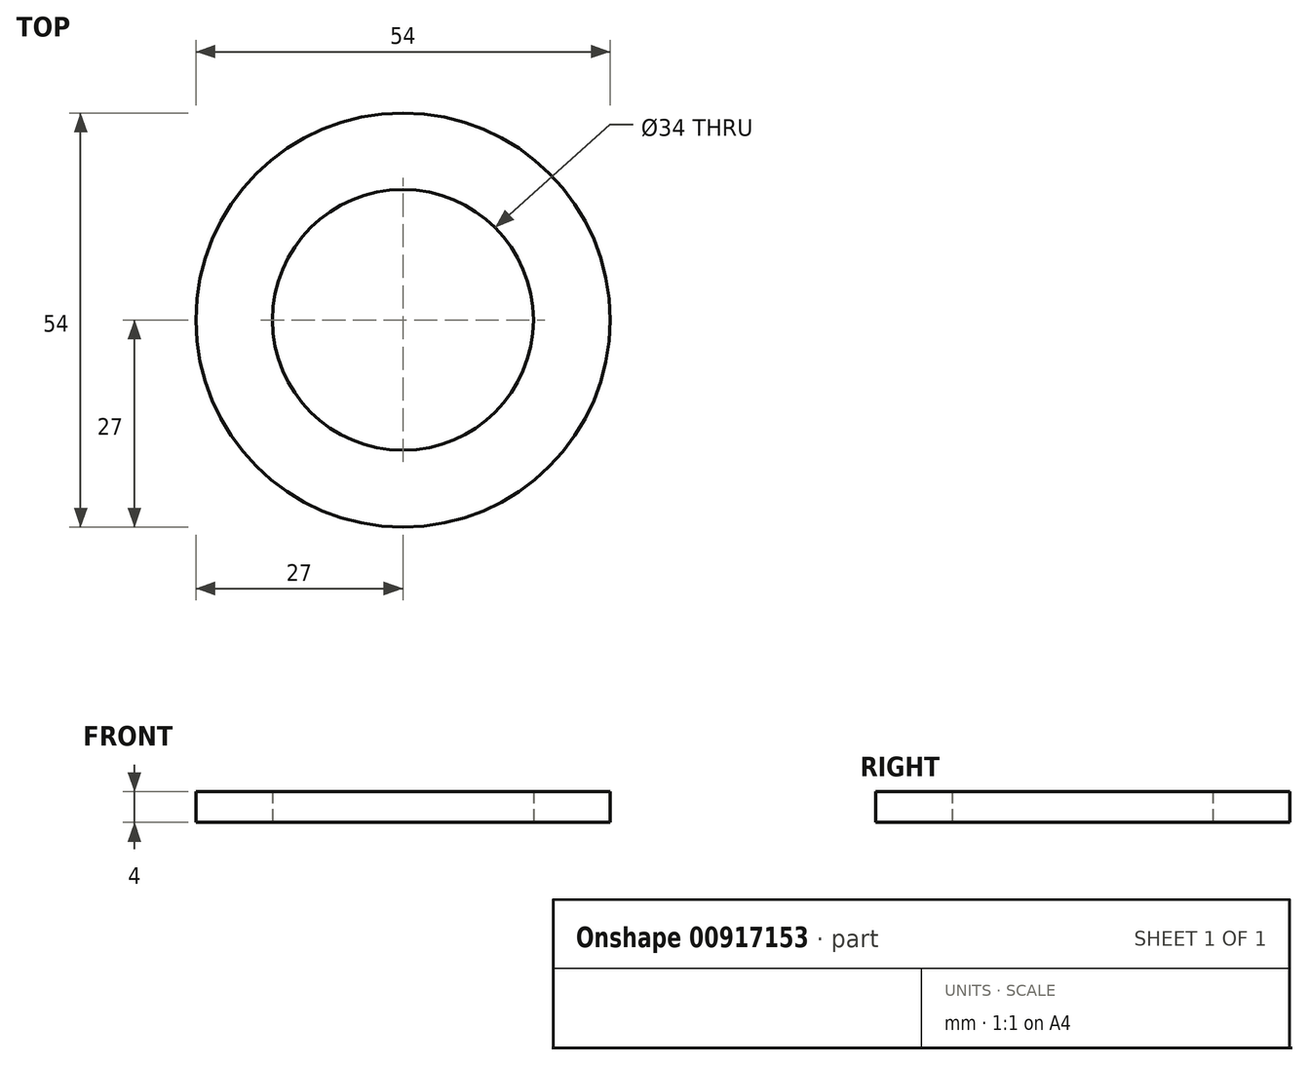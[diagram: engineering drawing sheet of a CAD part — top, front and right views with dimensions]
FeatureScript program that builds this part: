
annotation { "Feature Type Name" : "Feature", "Feature Type Description" : "" }
export const myFeature = defineFeature(function(context is Context, id is Id, definition is map)
    precondition{}
    {
        {
            var Q0;
            Q0=qCreatedBy(makeId("Top.planeOp"),FACE);
            var sketch = newSketch(context, id + "F0", { "sketchPlane" : qUnion([Q0])});
            skCircle(sketch, "E0", {"center": v(0, 0) * mm, "radius": 27 * mm});
            skCircle(sketch, "E1", {"center": v(0, 0) * mm, "radius": 17 * mm});
            skSolve(sketch);
        }
        {
            var Q0;
            Q0 = qSketchRegion(id + "F0", true);
            extrude(context, id + "F1", {"entities" : qUnion([Q0]), "depth" : 4 * mm, "offsetDistance" : 25 * mm});
        }
    });
